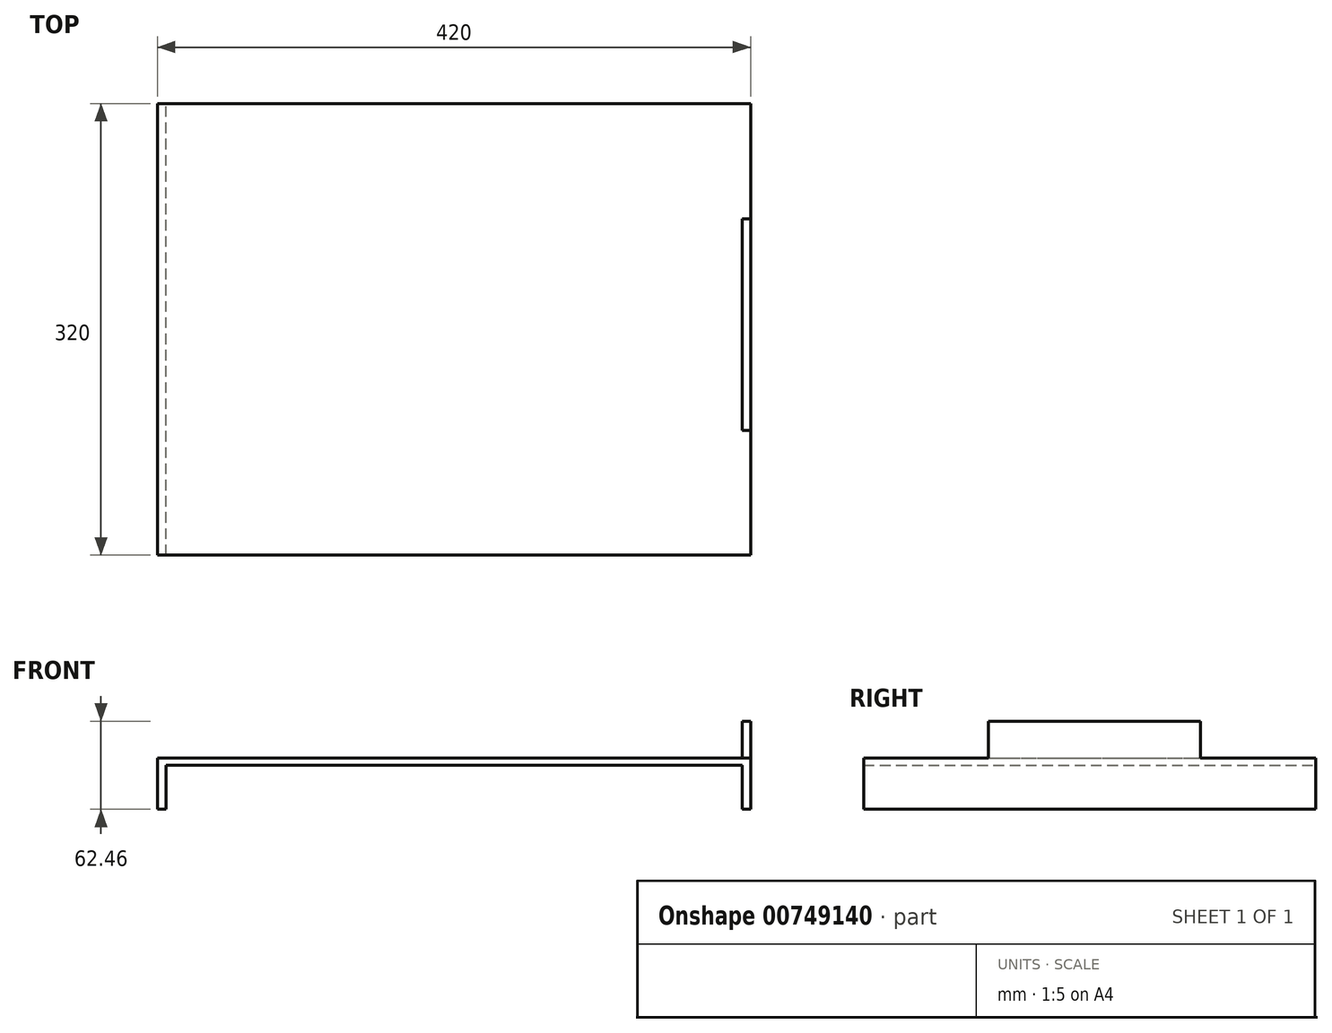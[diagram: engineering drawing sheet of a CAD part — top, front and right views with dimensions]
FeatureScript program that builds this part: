
annotation { "Feature Type Name" : "Feature", "Feature Type Description" : "" }
export const myFeature = defineFeature(function(context is Context, id is Id, definition is map)
    precondition{}
    {
        {
            var Q0;
            Q0=qCreatedBy(makeId("Front.planeOp"),FACE);
            var sketch = newSketch(context, id + "F0", { "sketchPlane" : qUnion([Q0])});
            skLineSegment(sketch, "E0", {"start": v(-210, -36.4) * mm, "end": v(-210, 0) * mm});
            skLineSegment(sketch, "E1", {"start": v(-210, 0) * mm, "end": v(0, 0) * mm});
            skLineSegment(sketch, "E2", {"start": v(-210, -36.4) * mm, "end": v(-204, -36.4) * mm});
            skLineSegment(sketch, "E3", {"start": v(-204, -36.4) * mm, "end": v(-204, -5.09) * mm});
            skLineSegment(sketch, "E4", {"start": v(-204, -5.09) * mm, "end": v(0, -5.09) * mm});
            skLineSegment(sketch, "E5.MirrorCS", {"start": v(210, 0) * mm, "end": v(0, 0) * mm});
            skLineSegment(sketch, "E6.MirrorCS", {"start": v(204, -5.09) * mm, "end": v(0, -5.09) * mm});
            skLineSegment(sketch, "E7.MirrorCS", {"start": v(204, -36.4) * mm, "end": v(204, -5.09) * mm});
            skLineSegment(sketch, "E8.MirrorCS", {"start": v(210, -36.4) * mm, "end": v(210, 0) * mm});
            skLineSegment(sketch, "E9.MirrorCS", {"start": v(210, -36.4) * mm, "end": v(204, -36.4) * mm});
            skSolve(sketch);
        }
        {
            var Q0;
            Q0=makeQuery(id+"F0.imprint","IMPRINT",FACE,{"disambiguationData":[TD([[makeQuery(id+"F0.imprint","IMPRINT",EDGE,{"derivedFrom":sQuery(id+"F0.wireOp",EDGE,"E0")}),-1.0]])]});
            extrude(context, id + "F1", {"entities" : qUnion([Q0]), "depth" : 320 * mm, "offsetDistance" : 25 * mm});
        }
        {
            var Q0;
            Q0=makeQuery(id+"F1.opExtrude","SWEPT_FACE",FACE,{"disambiguationData":[OSD([sQuery(id+"F0.wireOp",EDGE,"E8.MirrorCS")])]});
            var sketch = newSketch(context, id + "F2", { "sketchPlane" : qUnion([Q0])});
            skLineSegment(sketch, "E10", {"start": v(-160, 26.07) * mm, "end": v(-160, -67) * mm, "construction": true});
            skPoint(sketch, "E10.startSnap0", {"position": v(-160, 0) * mm});
            skPoint(sketch, "E10.endSnap0", {"position": v(-160, -36.4) * mm});
            skLineSegment(sketch, "E11", {"start": v(-231.6, 0) * mm, "end": v(-231.6, 26.07) * mm});
            skLineSegment(sketch, "E12", {"start": v(-231.6, 26.07) * mm, "end": v(-81.6, 26.07) * mm});
            skLineSegment(sketch, "E13", {"start": v(-81.6, 26.07) * mm, "end": v(-81.6, 0) * mm});
            skSolve(sketch);
        }
        {
            var Q0;
            {var subQ0=sQuery(id+"F2.wireOp",EDGE,"E11");Q0=makeQuery(id+"F2.imprint","IMPRINT",FACE,{"disambiguationData":[TD([[makeQuery(id+"F2.imprint","IMPRINT",EDGE,{"derivedFrom":subQ0}),-1.0]])]});}
            extrude(context, id + "F3", {"entities" : qUnion([Q0]), "operationType" : NewBodyOperationType.ADD, "oppositeDirection" : true, "depth" : 6 * mm, "offsetDistance" : 25 * mm});
        }
    });
